# Revit family: Rohrschelle Titan HD, M16, o.D
name_source: partatom
category: HLS-Bauteile
revit_build: Autodesk Revit 2017 (Build: 20190507_1515(x64)
units: mm (PartAtom-declared; Revit-internal decimal feet)

## family parameters
Arbeitsebenenbasiert = Ja
Beim Laden mit Abzugskörper schneiden = Nein
Bemaßung runder Anschluss = Durchmesser verwenden
Gemeinsam genutzt = Ja
Immer vertikal = Nein
Raumberechnungspunkt = Nein
Teiletyp = Normal

## types (21) — shared parameters
A = 20 mm  [stored 0.0656168 ft]
Anschluss = M16
Anschlußhöhe = 20 mm
Bauart = zweiteilig
Brandschutz = RAL GZ 656
DF1 = 29 mm  [stored 0.0951444 ft]
DVS = 13 mm
Fabrikat = MEFA
Firma = MEFA Befestigungs- und Montagesysteme GmbH
HGA = 15 mm  [stored 0.0492126 ft]
Kurztext1 = Rohrschelle Titan HD 50x5,0
MB = 50 mm  [stored 0.164042 ft]
MD = 5 mm  [stored 0.0164042 ft]
Material = Stahl
Materialmaße = 50x5,0 mm
Materialname = S235
Mengeneinheit = St
Oberflaeche = galvanisch verzinkt
Verschluss = Schraubverschluss
Verschluss-Schraube = M12
Vorgabe-Ansicht = 1219 mm
max. zul. Last horizontal = 0.00 kN
max. zul. Last vertikal = 0.00 kN
vpe = 1 St
zero-valued in all types: Nennweite DN Rohr, Stärke Material, max. Rohraußendurchmesser, min. Rohraußendurchmesser

## per-type parameters (varying)
| type | Achsabstand | Artikelnummer | B | Breite | D | DF2 | EAN | Gewicht | Gewicht pro Bauteil | H | Höhe | Kurztext2 | R | RM | Rohraußendurchmesser | Rohraußendurchmesser Zoll | S | max. Höhe | max. zul. Last |
| Titan HD, M16, Ø 64, o.D. | 112 mm | 0071515 | 141 mm | 141 mm | 64 mm  [stored 0.209974 ft] | 13 mm | 4250928403254 | 0.78 kg | 0.78 kg | 89 mm  [stored 0.291995 ft] | 89 mm | 64 mm M16 | 32 mm  [stored 0.104987 ft] | 37 mm  [stored 0.121391 ft] | 64 mm  [stored 0.209974 ft] | Zoll | 112 mm | 89 mm  [stored 0.291995 ft] | 6.00 kN |
| Titan HD, M16, Ø 76, o.D. | 124 mm | 0071519 | 154 mm | 153 mm | 76 mm  [stored 0.249344 ft] | 13 mm | 4250928403278 | 0.86 kg | 0.86 kg | 101 mm  [stored 0.331365 ft] | 101 mm | 76 mm M16 | 38 mm  [stored 0.124672 ft] | 43 mm | 76 mm  [stored 0.249344 ft] | 2 1/2 Zoll | 125 mm | 101 mm  [stored 0.331365 ft] | 6.00 kN |
| Titan HD, M16, Ø 89, o.D. | 138 mm | 0071521 | 167 mm | 167 mm | 89 mm  [stored 0.291995 ft] | 13 mm | 4250928403292 | 0.94 kg | 0.94 kg | 114 mm | 114 mm | 89 mm M16 | 45 mm | 50 mm  [stored 0.164042 ft] | 89 mm  [stored 0.291995 ft] | 3 Zoll | 138 mm | 114 mm | 6.00 kN |
| Titan HD, M16, Ø108, o.D. | 157 mm | 0071527 | 186 mm | 186 mm | 108 mm  [stored 0.354331 ft] | 13 mm | 4250928403315 | 1.06 kg | 1.06 kg | 133 mm | 133 mm | 108 mm M16 | 54 mm  [stored 0.177165 ft] | 59 mm  [stored 0.19357 ft] | 108 mm  [stored 0.354331 ft] | Zoll | 157 mm | 133 mm | 6.00 kN |
| Titan HD, M16, Ø110, o.D. | 159 mm | 0071529 | 188 mm | 188 mm | 110 mm  [stored 0.360892 ft] | 13 mm | 4250928403339 | 1.08 kg | 1.08 kg | 135 mm | 135 mm | 110 mm M16 | 55 mm  [stored 0.180446 ft] | 60 mm  [stored 0.19685 ft] | 110 mm  [stored 0.360892 ft] | Zoll | 159 mm | 135 mm | 6.00 kN |
| Titan HD, M16, Ø114, o.D. | 163 mm | 0071530 | 192 mm | 192 mm | 114 mm | 13 mm | 4250928403346 | 1.10 kg | 1.10 kg | 139 mm | 139 mm | 114 mm M16 | 57 mm  [stored 0.187008 ft] | 62 mm  [stored 0.203412 ft] | 114 mm | 4 Zoll | 163 mm | 139 mm | 6.00 kN |
| Titan HD, M16, Ø133, o.D. | 183 mm | 0071588 | 212 mm | 212 mm | 133 mm | 14 mm  [stored 0.0459318 ft] | 4250928403384 | 1.22 kg | 1.22 kg | 158 mm | 158 mm | 133 mm M16 | 67 mm | 72 mm | 133 mm | Zoll | 183 mm | 158 mm | 6.00 kN |
| Titan HD, M16, Ø135, o.D. | 185 mm | 0071596 | 214 mm | 214 mm | 135 mm | 14 mm  [stored 0.0459318 ft] | 4250928403407 | 1.23 kg | 1.23 kg | 160 mm | 160 mm | 135 mm M16 | 68 mm | 73 mm | 135 mm | Zoll | 185 mm | 160 mm | 6.00 kN |
| Titan HD, M16, Ø140, o.D. | 190 mm | 0071610 | 219 mm | 219 mm | 140 mm | 14 mm  [stored 0.0459318 ft] | 4250928403421 | 1.27 kg | 1.27 kg | 165 mm | 165 mm | 140 mm M16 | 70 mm  [stored 0.229659 ft] | 75 mm  [stored 0.246063 ft] | 140 mm | 5 Zoll | 190 mm | 165 mm | 6.00 kN |
| Titan HD, M16, Ø160, o.D. | 209 mm | 0071642 | 239 mm | 238 mm | 160 mm | 14 mm  [stored 0.0459318 ft] | 4250928403469 | 1.39 kg | 1.39 kg | 185 mm | 185 mm | 160 mm M16 | 80 mm  [stored 0.262467 ft] | 85 mm  [stored 0.278871 ft] | 160 mm | Zoll | 210 mm | 185 mm | 6.00 kN |
| Titan HD, M16, Ø165, o.D. | 215 mm | 0071685 | 244 mm | 244 mm | 165 mm | 14 mm  [stored 0.0459318 ft] | 4250928403483 | 1.43 kg | 1.43 kg | 190 mm | 190 mm | 165 mm M16 | 83 mm | 88 mm | 165 mm | 6 Zoll | 215 mm | 190 mm | 6.00 kN |
| Titan HD, M16, Ø168, o.D. | 218 mm | 0071687 | 247 mm | 247 mm | 168 mm | 14 mm  [stored 0.0459318 ft] | 4250928403490 | 1.44 kg | 1.44 kg | 193 mm | 193 mm | 168 mm M16 | 84 mm  [stored 0.275591 ft] | 89 mm  [stored 0.291995 ft] | 168 mm | Zoll | 218 mm | 193 mm | 6.00 kN |
| Titan HD, M16, Ø194, o.D. | 244 mm | 0071758 | 273 mm | 273 mm | 194 mm | 14 mm  [stored 0.0459318 ft] | 4250928403544 | 1.61 kg | 1.61 kg | 219 mm | 219 mm | 194 mm M16 | 97 mm  [stored 0.318241 ft] | 102 mm  [stored 0.334646 ft] | 194 mm | Zoll | 244 mm | 219 mm | 16.00 kN |
| Titan HD, M16, Ø200, o.D. | 249 mm | 0071774 | 279 mm | 278 mm | 200 mm | 14 mm  [stored 0.0459318 ft] | 4250928403568 | 1.65 kg | 1.65 kg | 225 mm | 225 mm | 200 mm M16 | 100 mm  [stored 0.328084 ft] | 105 mm  [stored 0.344488 ft] | 200 mm | Zoll | 250 mm | 225 mm | 16.00 kN |
| Titan HD, M16, Ø210, o.D. | 261 mm | 0071784 | 290 mm | 290 mm | 210 mm | 14 mm  [stored 0.0459318 ft] | 4250928403582 | 1.71 kg | 1.71 kg | 235 mm | 235 mm | 210 mm M16 | 105 mm  [stored 0.344488 ft] | 110 mm  [stored 0.360892 ft] | 210 mm | Zoll | 261 mm | 235 mm | 16.00 kN |
| Titan HD, M16, Ø219, o.D. | 270 mm | 0071804 | 299 mm | 299 mm | 219 mm | 14 mm  [stored 0.0459318 ft] | 4250928403605 | 1.77 kg | 1.77 kg | 244 mm | 244 mm | 219 mm M16 | 110 mm  [stored 0.360892 ft] | 115 mm | 219 mm | 8 Zoll | 270 mm | 244 mm | 16.00 kN |
| Titan HD, M16, Ø267, o.D. | 318 mm | 0071873 | 347 mm | 347 mm | 267 mm | 14 mm  [stored 0.0459318 ft] | 4250928403643 | 2.07 kg | 2.07 kg | 292 mm | 292 mm | 267 mm M16 | 134 mm | 139 mm | 267 mm | Zoll | 318 mm | 292 mm | 16.00 kN |
| Titan HD, M16, Ø273, o.D. | 324 mm | 0071898 | 353 mm | 353 mm | 273 mm | 14 mm  [stored 0.0459318 ft] | 4250928403667 | 2.11 kg | 2.11 kg | 298 mm | 298 mm | 273 mm M16 | 137 mm | 142 mm | 273 mm | 10 Zoll | 324 mm | 298 mm | 16.00 kN |
| Titan HD, M16, Ø324, o.D. | 375 mm | 0071939 | 404 mm | 404 mm | 324 mm | 14 mm  [stored 0.0459318 ft] | 4250928403704 | 2.44 kg | 2.44 kg | 349 mm | 349 mm | 324 mm M16 | 162 mm | 167 mm | 324 mm | 12 Zoll | 375 mm | 349 mm | 16.00 kN |
| Titan HD, M16, Ø356, o.D. | 407 mm | 0071977 | 436 mm | 436 mm | 356 mm | 14 mm  [stored 0.0459318 ft] | 4250928403728 | 2.64 kg | 2.64 kg | 381 mm | 381 mm | 356 mm M16 | 178 mm | 183 mm | 356 mm | Zoll | 407 mm | 381 mm | 16.00 kN |
| Titan HD, M16, Ø368, o.D. | 419 mm | 0071979 | 448 mm | 448 mm | 368 mm | 14 mm  [stored 0.0459318 ft] | 4250928403742 | 2.72 kg | 2.72 kg | 393 mm | 393 mm | 368 mm M16 | 184 mm | 189 mm | 368 mm | 14 Zoll | 419 mm | 393 mm | 16.00 kN |

note: [stored X ft] marks values corroborated as IEEE doubles in the binary element streams (Revit-internal decimal feet)

## geometry (parser evidence)
native form markers: Sweep x3
no freeform markers — native parametric forms only
